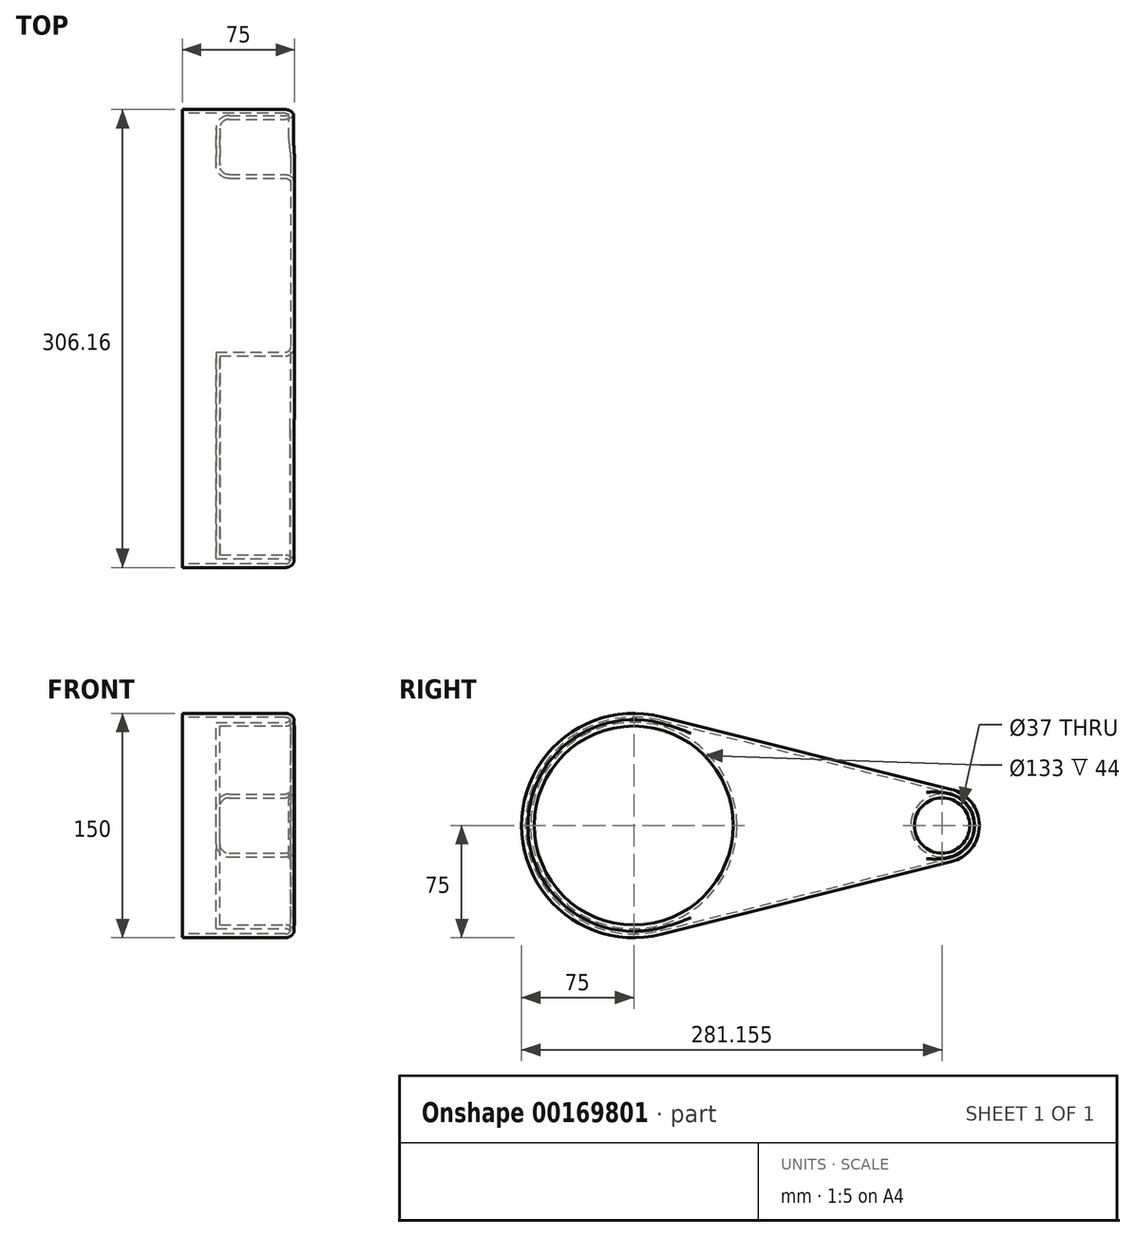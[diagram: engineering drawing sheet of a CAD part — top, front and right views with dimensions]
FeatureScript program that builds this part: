
annotation { "Feature Type Name" : "Feature", "Feature Type Description" : "" }
export const myFeature = defineFeature(function(context is Context, id is Id, definition is map)
    precondition{}
    {
        {
            var Q0;
            Q0=qCreatedBy(makeId("Right.planeOp"),FACE);
            var sketch = newSketch(context, id + "F0", { "sketchPlane" : qUnion([Q0])});
            skCircle(sketch, "E0", {"center": v(0, 0) * mm, "radius": 75 * mm});
            skCircle(sketch, "E1", {"center": v(206.16, 0) * mm, "radius": 25 * mm});
            skLineSegment(sketch, "E2", {"start": v(18.2, 72.76) * mm, "end": v(212.22, 24.25) * mm});
            skLineSegment(sketch, "E3", {"start": v(18.2, -72.76) * mm, "end": v(212.22, -24.25) * mm});
            skSolve(sketch);
        }
        {
            var Q0;
            {var subQ0=sQuery(id+"F0.wireOp",EDGE,"E0");var subQ1=makeQuery(id+"F0.imprint","INTERSECT",VERTEX,{"derivedFrom":[subQ0,sQuery(id+"F0.wireOp",EDGE,"E2")]});Q0=makeQuery(id+"F0.imprint","IMPRINT",FACE,{"disambiguationData":[TD([[makeQuery(id+"F0.imprint","IMPRINT",EDGE,{"disambiguationData":[TD([[subQ1,-1.0]])],"derivedFrom":subQ0}),1.0]])]});}
            var Q1;
            {var subQ0=sQuery(id+"F0.wireOp",EDGE,"E2");Q1=makeQuery(id+"F0.imprint","IMPRINT",FACE,{"disambiguationData":[TD([[makeQuery(id+"F0.imprint","IMPRINT",EDGE,{"derivedFrom":subQ0}),-1.0]])]});}
            var Q2;
            {var subQ0=sQuery(id+"F0.wireOp",EDGE,"E1");var subQ1=makeQuery(id+"F0.imprint","INTERSECT",VERTEX,{"derivedFrom":[subQ0,sQuery(id+"F0.wireOp",EDGE,"E2")]});Q2=makeQuery(id+"F0.imprint","IMPRINT",FACE,{"disambiguationData":[TD([[makeQuery(id+"F0.imprint","IMPRINT",EDGE,{"disambiguationData":[TD([[subQ1,-1.0]])],"derivedFrom":subQ0}),1.0]])]});}
            extrude(context, id + "F1", {"entities" : qUnion([Q0, Q1, Q2]), "depth" : 75 * mm});
        }
        {
            var Q0;
            Q0=makeQuery(id+"F1.opExtrude","CAP_FACE",FACE,{"disambiguationData":[OSD([sQuery(id+"F0.wireOp",EDGE,"E0"),sQuery(id+"F0.wireOp",EDGE,"E1"),sQuery(id+"F0.wireOp",EDGE,"E2"),sQuery(id+"F0.wireOp",EDGE,"E3")])],"isStart":false});
            var sketch = newSketch(context, id + "F2", { "sketchPlane" : qUnion([Q0])});
            skCircle(sketch, "E4", {"center": v(0, 0) * mm, "radius": 66.5 * mm});
            skCircle(sketch, "E5", {"center": v(206.16, 0) * mm, "radius": 18.5 * mm});
            skSolve(sketch);
        }
        {
            var Q0;
            Q0=makeQuery(id+"F2.imprint","IMPRINT",FACE,{"disambiguationData":[TD([[makeQuery(id+"F2.imprint","IMPRINT",EDGE,{"derivedFrom":sQuery(id+"F2.wireOp",EDGE,"E4")}),1.0]])]});
            var Q1;
            Q1=makeQuery(id+"F2.imprint","IMPRINT",FACE,{"disambiguationData":[TD([[makeQuery(id+"F2.imprint","IMPRINT",EDGE,{"derivedFrom":sQuery(id+"F2.wireOp",EDGE,"E5")}),1.0]])]});
            var Q2;
            Q2=sQuery(id+"F2.wireOp",EDGE,"E4");
            var Q3;
            Q3=sQuery(id+"F2.wireOp",EDGE,"E5");
            extrude(context, id + "F3", {"entities" : qUnion([Q0, Q1]), "operationType" : NewBodyOperationType.REMOVE, "surfaceEntities" : qUnion([Q2, Q3]), "oppositeDirection" : true, "depth" : 50 * mm});
        }
        {
            var Q0;
            Q0=makeQuery(id+"F1.opExtrude","CAP_FACE",FACE,{"disambiguationData":[OSD([sQuery(id+"F0.wireOp",EDGE,"E0"),sQuery(id+"F0.wireOp",EDGE,"E1"),sQuery(id+"F0.wireOp",EDGE,"E2"),sQuery(id+"F0.wireOp",EDGE,"E3")])],"isStart":false});
            var Q1;
            Q1=makeQuery(id+"F3.boolean.opBoolean","COPY",FACE,{"derivedFrom":makeQuery(id+"F3.opExtrude","CAP_FACE",FACE,{"disambiguationData":[OSD([sQuery(id+"F2.wireOp",EDGE,"E5")])],"isStart":false})});
            fillet(context, id + "F4", {"entities" : qUnion([Q0, Q1]), "radius" : 6 * mm, "tangentPropagation" : true, "allowEdgeOverflow" : false});
        }
        {
            var Q0;
            Q0=makeQuery(id+"F1.opExtrude","CAP_FACE",FACE,{"disambiguationData":[OSD([sQuery(id+"F0.wireOp",EDGE,"E0"),sQuery(id+"F0.wireOp",EDGE,"E1"),sQuery(id+"F0.wireOp",EDGE,"E2"),sQuery(id+"F0.wireOp",EDGE,"E3")])],"isStart":true});
            shell(context, id + "F5", {"entities" : qUnion([Q0]), "thickness" : 2.5 * mm});
        }
    });
